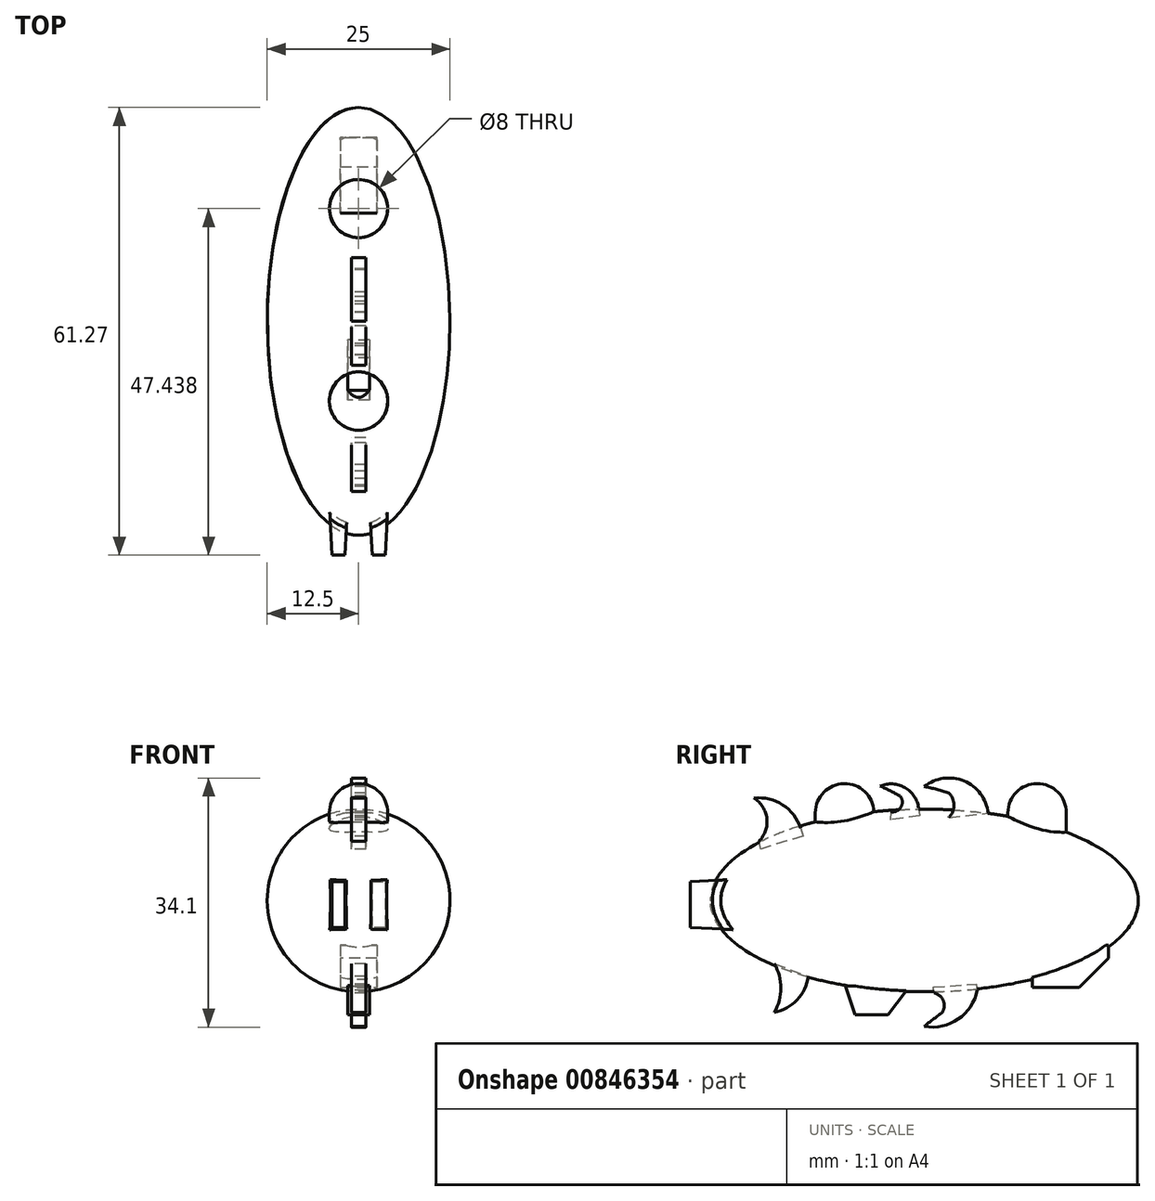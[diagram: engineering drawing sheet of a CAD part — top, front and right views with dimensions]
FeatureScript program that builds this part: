
annotation { "Feature Type Name" : "Feature", "Feature Type Description" : "" }
export const myFeature = defineFeature(function(context is Context, id is Id, definition is map)
    precondition{}
    {
        {
            var Q0;
            Q0=qCreatedBy(makeId("Top.planeOp"),FACE);
            var sketch = newSketch(context, id + "F0", { "sketchPlane" : qUnion([Q0])});
            skEllipse(sketch, "E0", {"center": v(0, 0) * mm, "majorRadius": 29.27 * mm, "minorRadius": 12.5 * mm, "majorAxis": v(0, 1)});
            skLineSegment(sketch, "E1", {"start": v(0, -29.27) * mm, "end": v(0, 29.27) * mm});
            skSolve(sketch);
        }
        {
            var Q0;
            {var subQ0=sQuery(id+"F0.wireOp",EDGE,"E1");Q0=makeQuery(id+"F0.imprint","IMPRINT",FACE,{"disambiguationData":[TD([[makeQuery(id+"F0.imprint","IMPRINT",EDGE,{"derivedFrom":subQ0}),1.0]])]});}
            var Q1;
            Q1=sQuery(id+"F0.wireOp",EDGE,"E1");
            revolve(context, id + "F1", {"surfaceOperationType" : NewSurfaceOperationType.NEW, "entities" : qUnion([Q0]), "axis" : qUnion([Q1]), "revolveType" : RevolveType.FULL});
        }
        {
            var Q0;
            Q0=qCreatedBy(makeId("Top.planeOp"),FACE);
            var sketch = newSketch(context, id + "F2", { "sketchPlane" : qUnion([Q0])});
            skCircle(sketch, "E2", {"center": v(0, 15.44) * mm, "radius": 4 * mm});
            skCircle(sketch, "E3", {"center": v(0, -10.9) * mm, "radius": 4 * mm});
            skSolve(sketch);
        }
        {
            var Q0;
            Q0 = qSketchRegion(id + "F2", true);
            extrude(context, id + "F3", {"entities" : qUnion([Q0]), "operationType" : NewBodyOperationType.ADD, "depth" : 12 * mm, "offsetDistance" : 25 * mm});
        }
        {
            var Q0;
            Q0=makeQuery(id+"F3.opExtrude","CAP_FACE",FACE,{"disambiguationData":[OSD([sQuery(id+"F2.wireOp",EDGE,"E2")])],"isStart":false});
            cPlane(context, id + "F4", {"entities" : qUnion([Q0]), "cplaneType" : CPlaneType.OFFSET, "offset" : 0 * mm, "width" : 150 * mm, "height" : 150 * mm});
        }
        {
            var Q0;
            Q0=qCreatedBy(id+"F4.planeOp",FACE);
            var sketch = newSketch(context, id + "F5", { "sketchPlane" : qUnion([Q0])});
            skCircle(sketch, "E4", {"center": v(0, 15.44) * mm, "radius": 4 * mm});
            skCircle(sketch, "E5", {"center": v(0, -10.9) * mm, "radius": 4 * mm});
            skLineSegment(sketch, "E6", {"start": v(0, -6.9) * mm, "end": v(0, -14.9) * mm});
            skLineSegment(sketch, "E7", {"start": v(0, 19.44) * mm, "end": v(0, 11.44) * mm});
            skSolve(sketch);
        }
        {
            var Q0;
            {var subQ0=sQuery(id+"F5.wireOp",EDGE,"E7");Q0=makeQuery(id+"F5.imprint","IMPRINT",FACE,{"disambiguationData":[TD([[makeQuery(id+"F5.imprint","IMPRINT",EDGE,{"derivedFrom":subQ0}),-1.0]])]});}
            var Q1;
            {var subQ0=sQuery(id+"F5.wireOp",EDGE,"E6");Q1=makeQuery(id+"F5.imprint","IMPRINT",FACE,{"disambiguationData":[TD([[makeQuery(id+"F5.imprint","IMPRINT",EDGE,{"derivedFrom":subQ0}),-1.0]])]});}
            var Q2;
            Q2=sQuery(id+"F5.wireOp",EDGE,"E7");
            revolve(context, id + "F6", {"operationType" : NewBodyOperationType.ADD, "surfaceOperationType" : NewSurfaceOperationType.NEW, "entities" : qUnion([Q0, Q1]), "axis" : qUnion([Q2]), "revolveType" : RevolveType.FULL});
        }
        {
            var Q0;
            Q0=qCreatedBy(makeId("Right.planeOp"),FACE);
            var sketch = newSketch(context, id + "F7", { "sketchPlane" : qUnion([Q0])});
            skArc(sketch, "E8", {"start": v(8.73, 11.95) * mm, "mid": v(5.44, 16.35) * mm, "end": v(0, 15.6) * mm});
            skArc(sketch, "E9", {"start": v(8.73, 11.95) * mm, "mid": v(4.56, 14.23) * mm, "end": v(0, 15.6) * mm});
            skArc(sketch, "E10", {"start": v(3.36, 11.37) * mm, "mid": v(4.05, 13.03) * mm, "end": v(3.36, 14.7) * mm});
            skLineSegment(sketch, "E11", {"start": v(3.36, 11.37) * mm, "end": v(8.73, 11.95) * mm});
            skArc(sketch, "E12", {"start": v(-0.77, 12.66) * mm, "mid": v(-2.66, 15.45) * mm, "end": v(-6.03, 15.65) * mm});
            skArc(sketch, "E13", {"start": v(-0.77, 12.66) * mm, "mid": v(-3.32, 14.3) * mm, "end": v(-6.03, 15.65) * mm});
            skArc(sketch, "E14", {"start": v(-4.55, 12.14) * mm, "mid": v(-3.18, 12.79) * mm, "end": v(-3.32, 14.3) * mm});
            skLineSegment(sketch, "E15", {"start": v(-4.55, 12.14) * mm, "end": v(-0.77, 12.66) * mm});
            skArc(sketch, "E16", {"start": v(-16.94, 9.85) * mm, "mid": v(-19.37, 13.08) * mm, "end": v(-23.3, 14) * mm});
            skArc(sketch, "E17", {"start": v(-23.3, 14) * mm, "mid": v(-20.38, 11.54) * mm, "end": v(-16.94, 9.85) * mm});
            skArc(sketch, "E18", {"start": v(-22.61, 8.1) * mm, "mid": v(-21.54, 11.22) * mm, "end": v(-23.3, 14) * mm});
            skLineSegment(sketch, "E19", {"start": v(-22.61, 8.1) * mm, "end": v(-16.94, 9.85) * mm});
            skArc(sketch, "E20", {"start": v(-20.5, -15.3) * mm, "mid": v(-17.4, -13.6) * mm, "end": v(-15.9, -10.4) * mm});
            skArc(sketch, "E21", {"start": v(-15.9, -10.4) * mm, "mid": v(-18.78, -12.3) * mm, "end": v(-20.5, -15.3) * mm});
            skArc(sketch, "E22", {"start": v(-20.5, -15.3) * mm, "mid": v(-19.62, -11.99) * mm, "end": v(-20.5, -8.67) * mm});
            skLineSegment(sketch, "E23", {"start": v(-20.5, -8.67) * mm, "end": v(-15.9, -10.4) * mm});
            skArc(sketch, "E24", {"start": v(0, -17.24) * mm, "mid": v(4.64, -16.24) * mm, "end": v(7.23, -12.26) * mm});
            skArc(sketch, "E25", {"start": v(7.23, -12.26) * mm, "mid": v(3.51, -14.6) * mm, "end": v(0, -17.24) * mm});
            skArc(sketch, "E26", {"start": v(2.38, -15.4) * mm, "mid": v(2.6, -13.73) * mm, "end": v(1.3, -12.66) * mm});
            skLineSegment(sketch, "E27", {"start": v(7.23, -12.26) * mm, "end": v(1.3, -12.66) * mm});
            skLineSegment(sketch, "E28", {"start": v(1.3, -12.66) * mm, "end": v(1.25, -11.86) * mm});
            skLineSegment(sketch, "E29", {"start": v(1.25, -11.86) * mm, "end": v(7.1, -11.46) * mm});
            skLineSegment(sketch, "E30", {"start": v(7.1, -11.46) * mm, "end": v(7.23, -12.26) * mm});
            skLineSegment(sketch, "E31", {"start": v(-0.77, 12.66) * mm, "end": v(-0.62, 11.6) * mm});
            skLineSegment(sketch, "E32", {"start": v(-0.62, 11.6) * mm, "end": v(-4.59, 11.04) * mm});
            skLineSegment(sketch, "E33", {"start": v(-4.59, 11.04) * mm, "end": v(-4.55, 12.14) * mm});
            skLineSegment(sketch, "E34", {"start": v(-16.94, 9.85) * mm, "end": v(-16.62, 8.82) * mm});
            skLineSegment(sketch, "E35", {"start": v(-16.62, 8.82) * mm, "end": v(-22.37, 7.05) * mm});
            skLineSegment(sketch, "E36", {"start": v(-22.37, 7.05) * mm, "end": v(-22.61, 8.1) * mm});
            skSolve(sketch);
        }
        {
            var Q0;
            {var subQ0=sQuery(id+"F7.wireOp",EDGE,"E20");Q0=makeQuery(id+"F7.imprint","IMPRINT",FACE,{"disambiguationData":[TD([[makeQuery(id+"F7.imprint","IMPRINT",EDGE,{"derivedFrom":subQ0}),1.0]])]});}
            var Q1;
            {var subQ0=sQuery(id+"F7.wireOp",EDGE,"E23");Q1=makeQuery(id+"F7.imprint","IMPRINT",FACE,{"disambiguationData":[TD([[makeQuery(id+"F7.imprint","IMPRINT",EDGE,{"derivedFrom":subQ0}),-1.0]])]});}
            var Q2;
            Q2=makeQuery(id+"F7.imprint","IMPRINT",FACE,{"disambiguationData":[TD([[makeQuery(id+"F7.imprint","IMPRINT",EDGE,{"derivedFrom":sQuery(id+"F7.wireOp",EDGE,"E27")}),-1.0]])]});
            var Q3;
            {var subQ2=sQuery(id+"F7.wireOp",EDGE,"E26");Q3=makeQuery(id+"F7.imprint","IMPRINT",FACE,{"disambiguationData":[TD([[makeQuery(id+"F7.imprint","IMPRINT",EDGE,{"derivedFrom":subQ2}),-1.0]])]});}
            var Q4;
            {var subQ0=sQuery(id+"F7.wireOp",EDGE,"E24");Q4=makeQuery(id+"F7.imprint","IMPRINT",FACE,{"disambiguationData":[TD([[makeQuery(id+"F7.imprint","IMPRINT",EDGE,{"derivedFrom":subQ0}),1.0]])]});}
            var Q5;
            {var subQ0=sQuery(id+"F7.wireOp",EDGE,"E8");Q5=makeQuery(id+"F7.imprint","IMPRINT",FACE,{"disambiguationData":[TD([[makeQuery(id+"F7.imprint","IMPRINT",EDGE,{"derivedFrom":subQ0}),1.0]])]});}
            var Q6;
            {var subQ2=sQuery(id+"F7.wireOp",EDGE,"E10");Q6=makeQuery(id+"F7.imprint","IMPRINT",FACE,{"disambiguationData":[TD([[makeQuery(id+"F7.imprint","IMPRINT",EDGE,{"derivedFrom":subQ2}),-1.0]])]});}
            var Q7;
            {var subQ0=sQuery(id+"F7.wireOp",EDGE,"E12");Q7=makeQuery(id+"F7.imprint","IMPRINT",FACE,{"disambiguationData":[TD([[makeQuery(id+"F7.imprint","IMPRINT",EDGE,{"derivedFrom":subQ0}),1.0]])]});}
            var Q8;
            {var subQ1=sQuery(id+"F7.wireOp",EDGE,"E13");var subQ3=sQuery(id+"F7.wireOp",EDGE,"E14");var subQ4=makeQuery(id+"F7.imprint","INTERSECT",VERTEX,{"derivedFrom":[subQ1,subQ3]});Q8=makeQuery(id+"F7.imprint","IMPRINT",FACE,{"disambiguationData":[TD([[makeQuery(id+"F7.imprint","IMPRINT",EDGE,{"disambiguationData":[TD([[subQ4,1.0]])],"derivedFrom":subQ3}),-1.0]])]});}
            var Q9;
            {var subQ0=sQuery(id+"F7.wireOp",EDGE,"E31");Q9=makeQuery(id+"F7.imprint","IMPRINT",FACE,{"disambiguationData":[TD([[makeQuery(id+"F7.imprint","IMPRINT",EDGE,{"derivedFrom":subQ0}),-1.0]])]});}
            var Q10;
            Q10=makeQuery(id+"F7.imprint","IMPRINT",FACE,{"disambiguationData":[TD([[makeQuery(id+"F7.imprint","IMPRINT",EDGE,{"derivedFrom":sQuery(id+"F7.wireOp",EDGE,"E19")}),-1.0]])]});
            var Q11;
            {var subQ0=sQuery(id+"F7.wireOp",EDGE,"E19");Q11=makeQuery(id+"F7.imprint","IMPRINT",FACE,{"disambiguationData":[TD([[makeQuery(id+"F7.imprint","IMPRINT",EDGE,{"derivedFrom":subQ0}),1.0]])]});}
            var Q12;
            {var subQ0=sQuery(id+"F7.wireOp",EDGE,"E16");Q12=makeQuery(id+"F7.imprint","IMPRINT",FACE,{"disambiguationData":[TD([[makeQuery(id+"F7.imprint","IMPRINT",EDGE,{"derivedFrom":subQ0}),1.0]])]});}
            extrude(context, id + "F8", {"entities" : qUnion([Q0, Q1, Q2, Q3, Q4, Q5, Q6, Q7, Q8, Q9, Q10, Q11, Q12]), "endBound" : BoundingType.SYMMETRIC, "depth" : 2 * mm, "offsetDistance" : 25 * mm});
        }
        {
            var Q0;
            Q0=qCreatedBy(makeId("Top.planeOp"),FACE);
            cPlane(context, id + "F9", {"entities" : qUnion([Q0]), "cplaneType" : CPlaneType.OFFSET, "offset" : 9 * mm, "oppositeDirection" : true, "width" : 150 * mm, "height" : 150 * mm});
        }
        {
            var Q0;
            Q0=qCreatedBy(id+"F9.planeOp",FACE);
            var sketch = newSketch(context, id + "F10", { "sketchPlane" : qUnion([Q0])});
            skLineSegment(sketch, "E37.bottom", {"start": v(-2.5, 14.8) * mm, "end": v(2.5, 14.8) * mm});
            skLineSegment(sketch, "E37.top", {"start": v(-2.5, 25.19) * mm, "end": v(2.5, 25.19) * mm});
            skLineSegment(sketch, "E37.left", {"start": v(-2.5, 14.8) * mm, "end": v(-2.5, 25.19) * mm});
            skLineSegment(sketch, "E37.right", {"start": v(2.5, 14.8) * mm, "end": v(2.5, 25.19) * mm});
            skPoint(sketch, "E37.middle", {"position": v(0, 20) * mm});
            skSolve(sketch);
        }
        {
            var Q0;
            Q0 = qSketchRegion(id + "F10", true);
            extrude(context, id + "F11", {"entities" : qUnion([Q0]), "operationType" : NewBodyOperationType.ADD, "endBound" : BoundingType.SYMMETRIC, "depth" : 5.75 * mm, "offsetDistance" : 25 * mm});
        }
        {
            var Q0;
            Q0=makeQuery(id+"F11.opExtrude","CAP_EDGE",EDGE,{"disambiguationData":[OSD([sQuery(id+"F10.wireOp",EDGE,"E37.top")])],"isStart":true});
            chamfer(context, id + "F12", {"entities" : qUnion([Q0]), "width" : 4 * mm, "tangentPropagation" : true});
        }
        {
            var Q0;
            Q0=qCreatedBy(makeId("Right.planeOp"),FACE);
            var sketch = newSketch(context, id + "F13", { "sketchPlane" : qUnion([Q0])});
            skLineSegment(sketch, "E38", {"start": v(-2.33, -12.15) * mm, "end": v(-5, -15.65) * mm});
            skLineSegment(sketch, "E39", {"start": v(-5, -15.65) * mm, "end": v(-9.46, -15.65) * mm});
            skLineSegment(sketch, "E40", {"start": v(-9.46, -15.65) * mm, "end": v(-10.79, -11.66) * mm});
            skLineSegment(sketch, "E41", {"start": v(-10.79, -11.66) * mm, "end": v(-2.33, -12.15) * mm});
            skSolve(sketch);
        }
        {
            var Q0;
            Q0=makeQuery(id+"F13.imprint","IMPRINT",FACE,{"disambiguationData":[TD([[makeQuery(id+"F13.imprint","IMPRINT",EDGE,{"derivedFrom":sQuery(id+"F13.wireOp",EDGE,"E38")}),-1.0]])]});
            extrude(context, id + "F14", {"entities" : qUnion([Q0]), "operationType" : NewBodyOperationType.ADD, "endBound" : BoundingType.SYMMETRIC, "depth" : 3 * mm, "offsetDistance" : 25 * mm});
        }
        {
            var Q0;
            Q0=qCreatedBy(makeId("Front.planeOp"),FACE);
            cPlane(context, id + "F15", {"entities" : qUnion([Q0]), "cplaneType" : CPlaneType.OFFSET, "offset" : 25 * mm, "width" : 150 * mm, "height" : 150 * mm});
        }
        {
            var Q0;
            Q0=qCreatedBy(id+"F15.planeOp",FACE);
            var sketch = newSketch(context, id + "F16", { "sketchPlane" : qUnion([Q0])});
            skLineSegment(sketch, "E42.bottom", {"start": v(1.5, -4.06) * mm, "end": v(4, -4.06) * mm});
            skLineSegment(sketch, "E42.top", {"start": v(1.5, 2.94) * mm, "end": v(4, 2.94) * mm});
            skLineSegment(sketch, "E42.left", {"start": v(1.5, -4.06) * mm, "end": v(1.5, 2.94) * mm});
            skLineSegment(sketch, "E42.right", {"start": v(4, -4.06) * mm, "end": v(4, 2.94) * mm});
            skLineSegment(sketch, "E43.bottom", {"start": v(-1.5, -4.06) * mm, "end": v(-4, -4.06) * mm});
            skLineSegment(sketch, "E43.top", {"start": v(-1.5, 2.94) * mm, "end": v(-4, 2.94) * mm});
            skLineSegment(sketch, "E43.left", {"start": v(-1.5, -4.06) * mm, "end": v(-1.5, 2.94) * mm});
            skLineSegment(sketch, "E43.right", {"start": v(-4, -4.06) * mm, "end": v(-4, 2.94) * mm});
            skSolve(sketch);
        }
        {
            var Q0;
            Q0 = qSketchRegion(id + "F16", true);
            extrude(context, id + "F17", {"entities" : qUnion([Q0]), "operationType" : NewBodyOperationType.ADD, "depth" : 7 * mm, "offsetDistance" : 25 * mm, "hasDraft" : true, "draftAngle" : 3 * degree, "draftPullDirection" : true});
        }
    });
